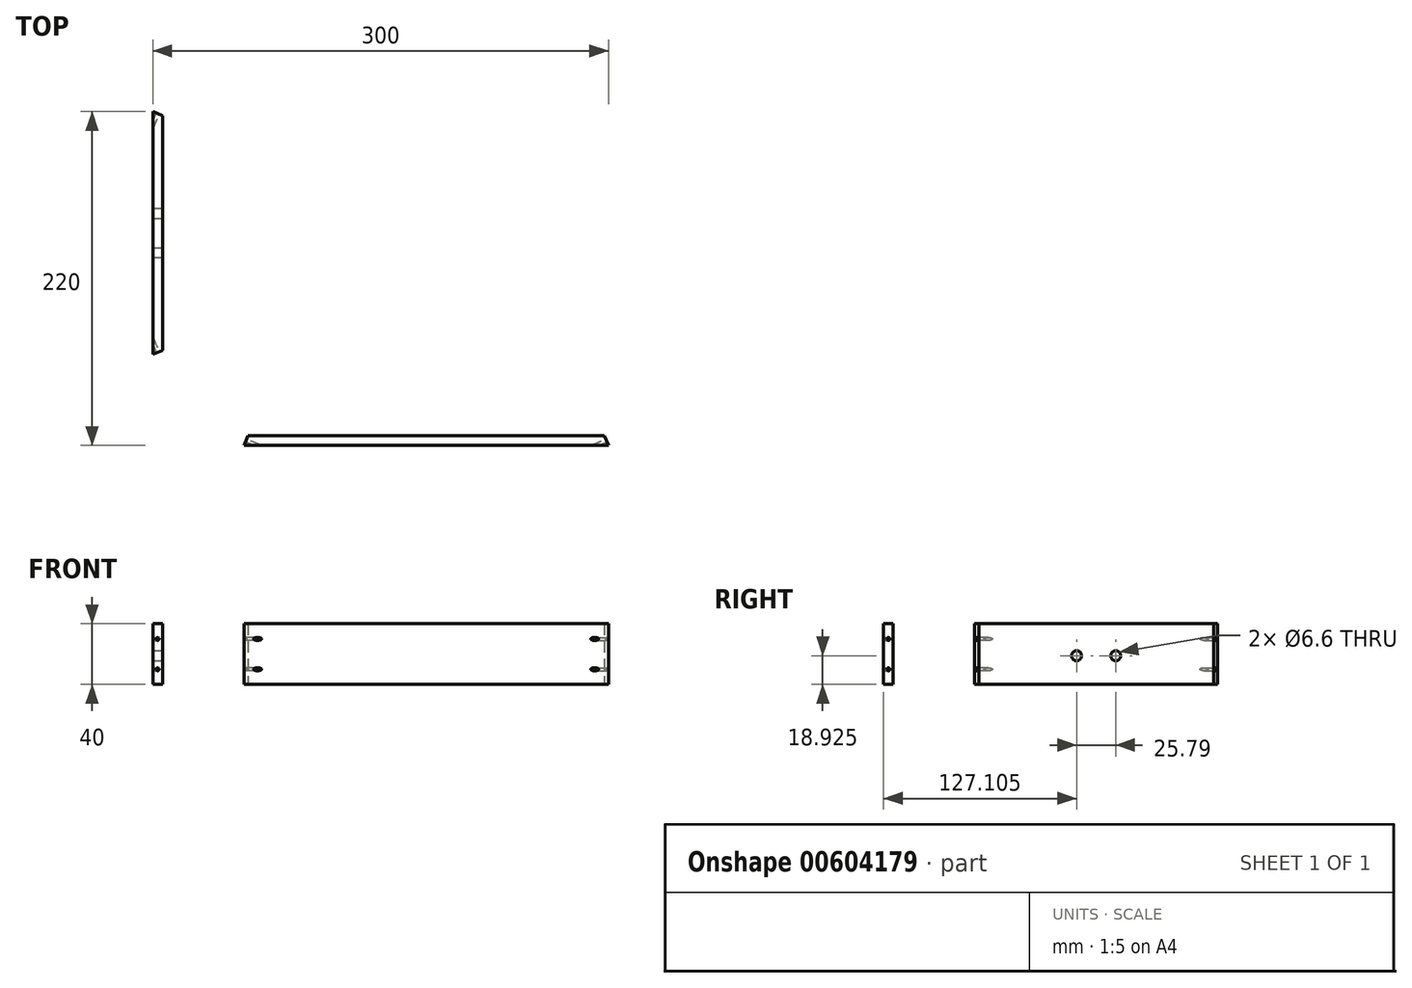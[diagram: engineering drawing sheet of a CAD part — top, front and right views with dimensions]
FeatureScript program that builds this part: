
annotation { "Feature Type Name" : "Feature", "Feature Type Description" : "" }
export const myFeature = defineFeature(function(context is Context, id is Id, definition is map)
    precondition{}
    {
        {
            var Q0;
            Q0=qCreatedBy(makeId("Top.planeOp"),FACE);
            var sketch = newSketch(context, id + "F0", { "sketchPlane" : qUnion([Q0])});
            skLineSegment(sketch, "E0", {"start": v(-120, 0) * mm, "end": v(-180, 60) * mm});
            skLineSegment(sketch, "E1", {"start": v(-180, 60) * mm, "end": v(-180, 220) * mm});
            skLineSegment(sketch, "E2", {"start": v(-180, 220) * mm, "end": v(-120, 280) * mm});
            skLineSegment(sketch, "E3", {"start": v(-120, 280) * mm, "end": v(120, 280) * mm});
            skLineSegment(sketch, "E4", {"start": v(120, 280) * mm, "end": v(180, 220) * mm});
            skLineSegment(sketch, "E5", {"start": v(180, 220) * mm, "end": v(180, 60) * mm});
            skLineSegment(sketch, "E6", {"start": v(180, 60) * mm, "end": v(120, 0) * mm});
            skLineSegment(sketch, "E7", {"start": v(120, 0) * mm, "end": v(-120, 0) * mm});
            skLineSegment(sketch, "E8.0", {"start": v(-173.65, 62.63) * mm, "end": v(-173.65, 217.37) * mm});
            skLineSegment(sketch, "E8.1", {"start": v(-117.37, 6.35) * mm, "end": v(-173.65, 62.63) * mm});
            skLineSegment(sketch, "E8.2", {"start": v(-173.65, 217.37) * mm, "end": v(-117.37, 273.65) * mm});
            skLineSegment(sketch, "E8.3", {"start": v(117.37, 6.35) * mm, "end": v(-117.37, 6.35) * mm});
            skLineSegment(sketch, "E8.4", {"start": v(-117.37, 273.65) * mm, "end": v(117.37, 273.65) * mm});
            skLineSegment(sketch, "E8.5", {"start": v(117.37, 273.65) * mm, "end": v(173.65, 217.37) * mm});
            skLineSegment(sketch, "E8.6", {"start": v(173.65, 217.37) * mm, "end": v(173.65, 62.63) * mm});
            skLineSegment(sketch, "E8.7", {"start": v(173.65, 62.63) * mm, "end": v(117.37, 6.35) * mm});
            skLineSegment(sketch, "E9", {"start": v(-120, 0) * mm, "end": v(-117.37, 6.35) * mm});
            skLineSegment(sketch, "E10", {"start": v(-120, 280) * mm, "end": v(-117.37, 273.65) * mm});
            skLineSegment(sketch, "E11", {"start": v(120, 280) * mm, "end": v(117.37, 273.65) * mm});
            skLineSegment(sketch, "E12", {"start": v(120, 0) * mm, "end": v(117.37, 6.35) * mm});
            skLineSegment(sketch, "E13", {"start": v(-173.65, 217.37) * mm, "end": v(-180, 220) * mm});
            skLineSegment(sketch, "E14", {"start": v(-173.65, 62.63) * mm, "end": v(-180, 60) * mm});
            skLineSegment(sketch, "E15", {"start": v(173.65, 62.63) * mm, "end": v(180, 60) * mm});
            skLineSegment(sketch, "E16", {"start": v(173.65, 217.37) * mm, "end": v(180, 220) * mm});
            skSolve(sketch);
        }
        {
            var Q0;
            Q0=makeQuery(id+"F0.imprint","IMPRINT",FACE,{"disambiguationData":[TD([[makeQuery(id+"F0.imprint","IMPRINT",EDGE,{"derivedFrom":sQuery(id+"F0.wireOp",EDGE,"E3")}),-1.0]])]});
            extrude(context, id + "F1", {"entities" : qUnion([Q0]), "depth" : 40 * mm, "offsetDistance" : 25 * mm});
        }
        {
            var Q0;
            Q0=makeQuery(id+"F0.imprint","IMPRINT",FACE,{"disambiguationData":[TD([[makeQuery(id+"F0.imprint","IMPRINT",EDGE,{"derivedFrom":sQuery(id+"F0.wireOp",EDGE,"E1")}),-1.0]])]});
            extrude(context, id + "F2", {"entities" : qUnion([Q0]), "depth" : 40 * mm, "offsetDistance" : 25 * mm});
        }
        {
            var Q0;
            Q0=makeQuery(id+"F0.imprint","IMPRINT",FACE,{"disambiguationData":[TD([[makeQuery(id+"F0.imprint","IMPRINT",EDGE,{"derivedFrom":sQuery(id+"F0.wireOp",EDGE,"E5")}),-1.0]])]});
            extrude(context, id + "F3", {"entities" : qUnion([Q0]), "depth" : 40 * mm, "offsetDistance" : 25 * mm});
        }
        {
            var Q0;
            Q0=makeQuery(id+"F0.imprint","IMPRINT",FACE,{"disambiguationData":[TD([[makeQuery(id+"F0.imprint","IMPRINT",EDGE,{"derivedFrom":sQuery(id+"F0.wireOp",EDGE,"E7")}),-1.0]])]});
            extrude(context, id + "F4", {"entities" : qUnion([Q0]), "depth" : 40 * mm, "offsetDistance" : 25 * mm});
        }
        {
            var Q0;
            Q0=makeQuery(id+"F2.opExtrude","SWEPT_FACE",FACE,{"disambiguationData":[OSD([sQuery(id+"F0.wireOp",EDGE,"E8.0")])]});
            var sketch = newSketch(context, id + "F5", { "sketchPlane" : qUnion([Q0])});
            skLineSegment(sketch, "E17", {"start": v(140, 40) * mm, "end": v(140, 0) * mm, "construction": true});
            skLineSegment(sketch, "E18.bottom", {"start": v(127.1, 40) * mm, "end": v(152.9, 40) * mm, "construction": true});
            skLineSegment(sketch, "E18.top", {"start": v(127.1, 18.93) * mm, "end": v(152.9, 18.92) * mm, "construction": true});
            skLineSegment(sketch, "E18.left", {"start": v(127.1, 40) * mm, "end": v(127.1, 18.93) * mm, "construction": true});
            skLineSegment(sketch, "E18.right", {"start": v(152.9, 40) * mm, "end": v(152.9, 18.93) * mm, "construction": true});
            skSolve(sketch);
        }
        {
            var Q0;
            Q0=sQuery(id+"F5.wireOp",VERTEX,"E18.top.start");
            var Q1;
            Q1=sQuery(id+"F5.wireOp",VERTEX,"E18.top.end");
            var Q2;
            Q2=makeQuery(id+"F2.opExtrude","SWEPT_BODY",BODY,{"disambiguationData":[OSD([sQuery(id+"F0.wireOp",EDGE,"E1"),sQuery(id+"F0.wireOp",EDGE,"E8.0"),sQuery(id+"F0.wireOp",EDGE,"E13"),sQuery(id+"F0.wireOp",EDGE,"E14")])]});
            hole(context, id + "F6", {"style" : HoleStyle.SIMPLE, "endStyle" : HoleEndStyle.THROUGH, "standardTappedOrClearance" : lookupTablePath({ "standard" : "ISO", "fit" : "Normal", "size" : "M6", "type" : "Clearance" }), "standardBlindInLast" : lookupTablePath({ "fit" : "Standard", "standard" : "ISO", "size" : "M6", "type" : "Clearance" }), "holeDiameter" : 6.6 * mm, "majorDiameter" : 5 * mm, "isTappedThrough" : true, "tappedDepth" : 12 * mm, "tapClearance" : 3, "locations" : qUnion([Q0, Q1]), "scope" : qUnion([Q2])});
        }
        {
            var Q0;
            Q0=makeQuery(id+"F3.opExtrude","SWEPT_FACE",FACE,{"disambiguationData":[OSD([sQuery(id+"F0.wireOp",EDGE,"E8.6")])]});
            var sketch = newSketch(context, id + "F7", { "sketchPlane" : qUnion([Q0])});
            skLineSegment(sketch, "E19", {"start": v(-140, 40) * mm, "end": v(-140, 0) * mm, "construction": true});
            skLineSegment(sketch, "E20.bottom", {"start": v(-152.9, 40) * mm, "end": v(-127.1, 40) * mm, "construction": true});
            skLineSegment(sketch, "E20.top", {"start": v(-152.9, 20) * mm, "end": v(-127.1, 20) * mm, "construction": true});
            skLineSegment(sketch, "E20.left", {"start": v(-152.9, 40) * mm, "end": v(-152.9, 20) * mm, "construction": true});
            skLineSegment(sketch, "E20.right", {"start": v(-127.1, 40) * mm, "end": v(-127.1, 20) * mm, "construction": true});
            skSolve(sketch);
        }
        {
            var Q0;
            Q0=sQuery(id+"F7.wireOp",VERTEX,"E20.right.end");
            var Q1;
            Q1=sQuery(id+"F7.wireOp",VERTEX,"E20.left.end");
            var Q2;
            Q2=makeQuery(id+"F3.opExtrude","SWEPT_BODY",BODY,{"disambiguationData":[OSD([sQuery(id+"F0.wireOp",EDGE,"E5"),sQuery(id+"F0.wireOp",EDGE,"E8.6"),sQuery(id+"F0.wireOp",EDGE,"E15"),sQuery(id+"F0.wireOp",EDGE,"E16")])]});
            hole(context, id + "F8", {"style" : HoleStyle.SIMPLE, "endStyle" : HoleEndStyle.THROUGH, "standardTappedOrClearance" : lookupTablePath({ "standard" : "ISO", "fit" : "Normal", "size" : "M6", "type" : "Clearance" }), "standardBlindInLast" : lookupTablePath({ "fit" : "Standard", "standard" : "ISO", "size" : "M6", "type" : "Clearance" }), "holeDiameter" : 6.6 * mm, "majorDiameter" : 5 * mm, "isTappedThrough" : true, "tappedDepth" : 12 * mm, "tapClearance" : 3, "locations" : qUnion([Q0, Q1]), "scope" : qUnion([Q2])});
        }
        {
            var Q0;
            Q0=makeQuery(id+"F4.opExtrude","SWEPT_FACE",FACE,{"disambiguationData":[OSD([sQuery(id+"F0.wireOp",EDGE,"E12")])]});
            var sketch = newSketch(context, id + "F9", { "sketchPlane" : qUnion([Q0])});
            skLineSegment(sketch, "E21", {"start": v(-42.49, 40) * mm, "end": v(-42.49, 30) * mm, "construction": true});
            skLineSegment(sketch, "E22", {"start": v(-42.49, 0) * mm, "end": v(-42.49, 10) * mm, "construction": true});
            skSolve(sketch);
        }
        {
            var Q0;
            Q0=makeQuery(id+"F2.opExtrude","SWEPT_FACE",FACE,{"disambiguationData":[OSD([sQuery(id+"F0.wireOp",EDGE,"E14")])]});
            var sketch = newSketch(context, id + "F10", { "sketchPlane" : qUnion([Q0])});
            skLineSegment(sketch, "E23", {"start": v(-139.9, 40) * mm, "end": v(-139.9, 30) * mm, "construction": true});
            skLineSegment(sketch, "E24", {"start": v(-139.9, 0) * mm, "end": v(-139.9, 10) * mm, "construction": true});
            skSolve(sketch);
        }
        {
            var Q0;
            Q0=makeQuery(id+"F2.opExtrude","SWEPT_FACE",FACE,{"disambiguationData":[OSD([sQuery(id+"F0.wireOp",EDGE,"E13")])]});
            var sketch = newSketch(context, id + "F11", { "sketchPlane" : qUnion([Q0])});
            skLineSegment(sketch, "E25", {"start": v(247.05, 40) * mm, "end": v(247.05, 30) * mm, "construction": true});
            skLineSegment(sketch, "E26", {"start": v(247.05, 0) * mm, "end": v(247.05, 10) * mm, "construction": true});
            skSolve(sketch);
        }
        {
            var Q0;
            Q0=makeQuery(id+"F1.opExtrude","SWEPT_BODY",BODY,{"disambiguationData":[OSD([sQuery(id+"F0.wireOp",EDGE,"E3"),sQuery(id+"F0.wireOp",EDGE,"E8.4"),sQuery(id+"F0.wireOp",EDGE,"E10"),sQuery(id+"F0.wireOp",EDGE,"E11")])]});
            var Q1;
            Q1=makeQuery(id+"F3.opExtrude","SWEPT_BODY",BODY,{"disambiguationData":[OSD([sQuery(id+"F0.wireOp",EDGE,"E5"),sQuery(id+"F0.wireOp",EDGE,"E8.6"),sQuery(id+"F0.wireOp",EDGE,"E15"),sQuery(id+"F0.wireOp",EDGE,"E16")])]});
            deleteBodies(context, id + "F12", {"entities" : qUnion([Q0, Q1])});
        }
        {
            var Q0;
            Q0=makeQuery(id+"F4.opExtrude","SWEPT_FACE",FACE,{"disambiguationData":[OSD([sQuery(id+"F0.wireOp",EDGE,"E9")])]});
            var sketch = newSketch(context, id + "F13", { "sketchPlane" : qUnion([Q0])});
            skLineSegment(sketch, "E27", {"start": v(42.49, 40) * mm, "end": v(42.49, 30) * mm, "construction": true});
            skLineSegment(sketch, "E28", {"start": v(42.49, 0) * mm, "end": v(42.49, 10) * mm, "construction": true});
            skSolve(sketch);
        }
        {
            var Q0;
            Q0=sQuery(id+"F9.wireOp",VERTEX,"E21.end");
            var Q1;
            Q1=sQuery(id+"F9.wireOp",VERTEX,"E22.end");
            var Q2;
            Q2=sQuery(id+"F13.wireOp",VERTEX,"E27.end");
            var Q3;
            Q3=sQuery(id+"F13.wireOp",VERTEX,"E28.end");
            var Q4;
            Q4=sQuery(id+"F10.wireOp",VERTEX,"E23.end");
            var Q5;
            Q5=sQuery(id+"F10.wireOp",VERTEX,"E24.end");
            var Q6;
            Q6=sQuery(id+"F11.wireOp",VERTEX,"E25.end");
            var Q7;
            Q7=sQuery(id+"F11.wireOp",VERTEX,"E26.end");
            var Q8;
            Q8=makeQuery(id+"F2.opExtrude","SWEPT_BODY",BODY,{"disambiguationData":[OSD([sQuery(id+"F0.wireOp",EDGE,"E1"),sQuery(id+"F0.wireOp",EDGE,"E8.0"),sQuery(id+"F0.wireOp",EDGE,"E13"),sQuery(id+"F0.wireOp",EDGE,"E14")])]});
            var Q9;
            Q9=makeQuery(id+"F4.opExtrude","SWEPT_BODY",BODY,{"disambiguationData":[OSD([sQuery(id+"F0.wireOp",EDGE,"E7"),sQuery(id+"F0.wireOp",EDGE,"E8.3"),sQuery(id+"F0.wireOp",EDGE,"E9"),sQuery(id+"F0.wireOp",EDGE,"E12")])]});
            hole(context, id + "F14", {"style" : HoleStyle.SIMPLE, "endStyle" : HoleEndStyle.THROUGH, "standardTappedOrClearance" : lookupTablePath({ "standard" : "ANSI", "engagement" : "75%", "pitch" : "48 tpi", "size" : "#3", "type" : "Tapped" }), "standardBlindInLast" : lookupTablePath({ "standard" : "ANSI", "engagement" : "75%", "pitch" : "48 tpi", "size" : "#3", "type" : "Tapped" }), "holeDiameter" : 2 * mm, "majorDiameter" : 2.5 * mm, "showTappedDepth" : true, "isTappedThrough" : true, "tappedDepth" : 12 * mm, "tapClearance" : 3, "locations" : qUnion([Q0, Q1, Q2, Q3, Q4, Q5, Q6, Q7]), "scope" : qUnion([Q8, Q9])});
        }
    });
